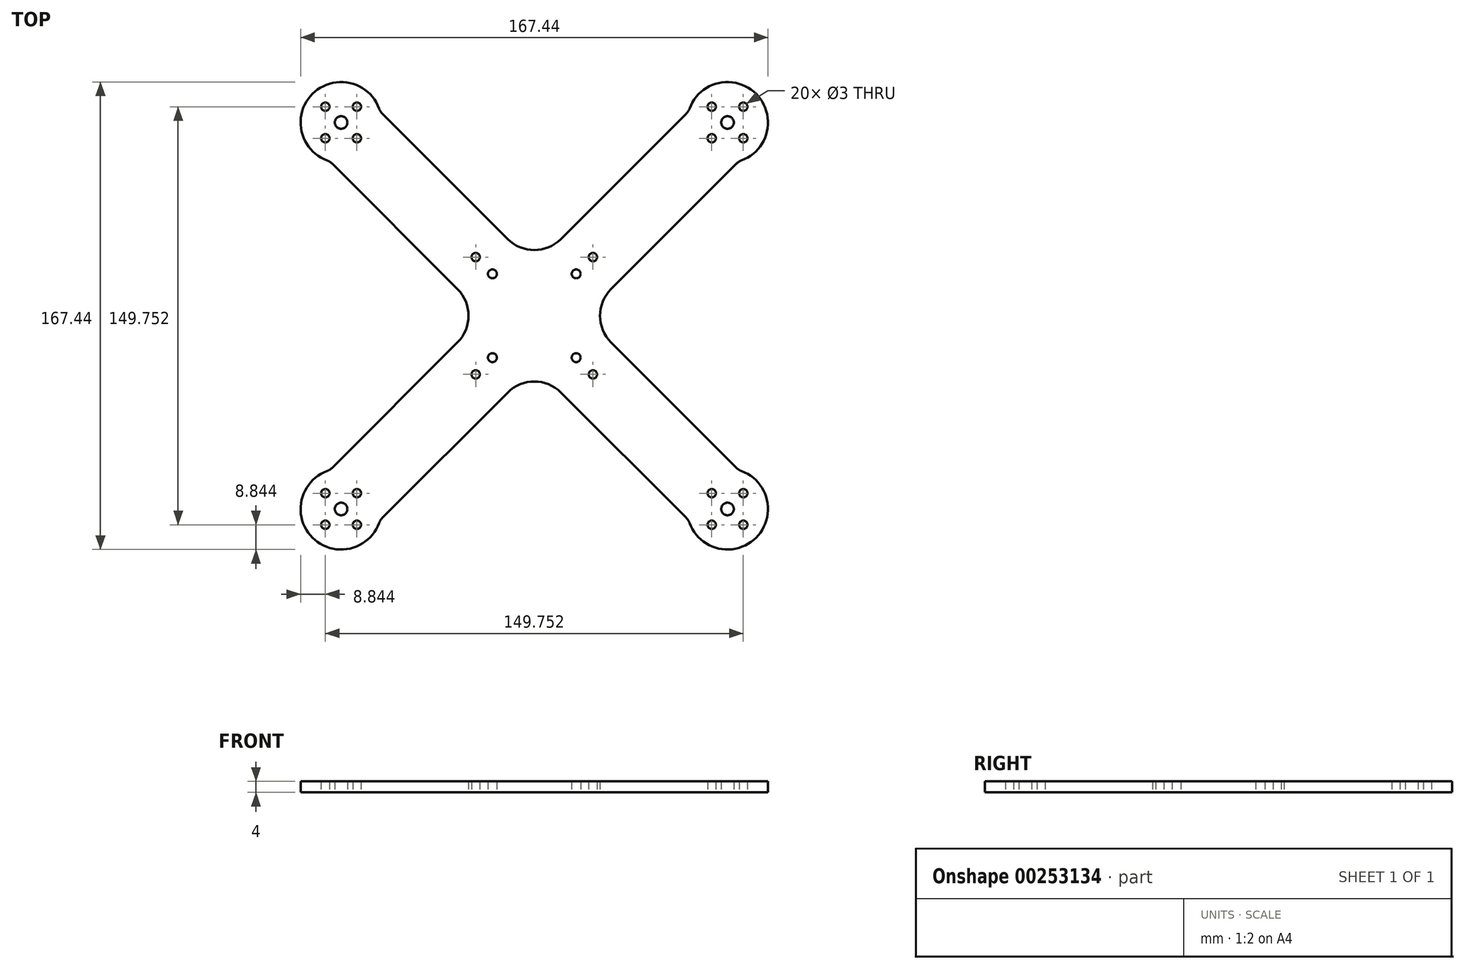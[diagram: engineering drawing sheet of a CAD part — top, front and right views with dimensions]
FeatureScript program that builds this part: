
annotation { "Feature Type Name" : "Feature", "Feature Type Description" : "" }
export const myFeature = defineFeature(function(context is Context, id is Id, definition is map)
    precondition{}
    {
        {
            var Q0;
            Q0=qCreatedBy(makeId("Top.planeOp"),FACE);
            var sketch = newSketch(context, id + "F0", { "sketchPlane" : qUnion([Q0])});
            skLineSegment(sketch, "E0.bottom", {"start": v(15, 15) * mm, "end": v(-15, 15) * mm, "construction": true});
            skLineSegment(sketch, "E0.left", {"start": v(15, 15) * mm, "end": v(15, -15) * mm, "construction": true});
            skLineSegment(sketch, "E0.right", {"start": v(-15, 15) * mm, "end": v(-15, -15) * mm, "construction": true});
            skCircle(sketch, "E1", {"center": v(-15, 15) * mm, "radius": 1.6 * mm});
            skCircle(sketch, "E2", {"center": v(15, 15) * mm, "radius": 1.6 * mm});
            skCircle(sketch, "E3", {"center": v(15, -15) * mm, "radius": 1.6 * mm});
            skCircle(sketch, "E4", {"center": v(-15, -15) * mm, "radius": 1.6 * mm});
            skLineSegment(sketch, "E5", {"start": v(-15, -15) * mm, "end": v(15, -15) * mm, "construction": true});
            skLineSegment(sketch, "E6", {"start": v(-15, 15) * mm, "end": v(15, -15) * mm, "construction": true});
            skLineSegment(sketch, "E7", {"start": v(-15, -15) * mm, "end": v(0, 0) * mm, "construction": true});
            skLineSegment(sketch, "E8.bottom", {"start": v(18, -18) * mm, "end": v(-18, -18) * mm, "construction": true});
            skLineSegment(sketch, "E8.top", {"start": v(18, 18) * mm, "end": v(-18, 18) * mm, "construction": true});
            skLineSegment(sketch, "E8.left", {"start": v(18, -18) * mm, "end": v(18, 18) * mm, "construction": true});
            skLineSegment(sketch, "E8.right", {"start": v(-18, -18) * mm, "end": v(-18, 18) * mm, "construction": true});
            skPoint(sketch, "E8.middle", {"position": v(0, 0) * mm});
            skLineSegment(sketch, "E9.bottom", {"start": v(21, 21) * mm, "end": v(-21, 21) * mm, "construction": true});
            skLineSegment(sketch, "E9.top", {"start": v(21, -21) * mm, "end": v(-21, -21) * mm, "construction": true});
            skLineSegment(sketch, "E9.left", {"start": v(21, 21) * mm, "end": v(21, -21) * mm, "construction": true});
            skLineSegment(sketch, "E9.right", {"start": v(-21, 21) * mm, "end": v(-21, -21) * mm, "construction": true});
            skCircle(sketch, "E10", {"center": v(21, 21) * mm, "radius": 1.5 * mm});
            skCircle(sketch, "E11", {"center": v(-21, 21) * mm, "radius": 1.5 * mm});
            skCircle(sketch, "E12", {"center": v(-21, -21) * mm, "radius": 1.5 * mm});
            skCircle(sketch, "E13", {"center": v(21, -21) * mm, "radius": 1.5 * mm});
            skPoint(sketch, "E14.visualSharp", {"position": v(-27.5, 27.5) * mm});
            skPoint(sketch, "E15.visualSharp", {"position": v(27.5, 27.5) * mm});
            skPoint(sketch, "E16.visualSharp", {"position": v(27.5, -27.5) * mm});
            skPoint(sketch, "E17.visualSharp", {"position": v(-27.5, -27.5) * mm});
            skLineSegment(sketch, "E18", {"start": v(-27.5, -27.5) * mm, "end": v(-69.22, -69.22) * mm, "construction": true});
            skCircle(sketch, "E19", {"center": v(-69.22, -69.22) * mm, "radius": 2.25 * mm});
            skLineSegment(sketch, "E20", {"start": v(-69.22, -69.22) * mm, "end": v(-63.56, -74.88) * mm, "construction": true});
            skLineSegment(sketch, "E21", {"start": v(-69.22, -69.22) * mm, "end": v(-74.88, -74.88) * mm, "construction": true});
            skLineSegment(sketch, "E22", {"start": v(-69.22, -69.22) * mm, "end": v(-74.88, -63.56) * mm, "construction": true});
            skCircle(sketch, "E23", {"center": v(-74.88, -63.56) * mm, "radius": 1.5 * mm});
            skCircle(sketch, "E24", {"center": v(-74.88, -74.88) * mm, "radius": 1.5 * mm});
            skCircle(sketch, "E25", {"center": v(-63.56, -74.88) * mm, "radius": 1.5 * mm});
            skCircle(sketch, "E26", {"center": v(-63.56, -63.56) * mm, "radius": 1.5 * mm});
            skArc(sketch, "E27", {"start": v(-74.22, -55.61) * mm, "mid": v(-79.47, -79.47) * mm, "end": v(-55.61, -74.22) * mm});
            skLineSegment(sketch, "E28.0", {"start": v(-27.5, -9.54) * mm, "end": v(-72.41, -54.45) * mm});
            skLineSegment(sketch, "E29.0", {"start": v(-9.54, -27.5) * mm, "end": v(-54.45, -72.41) * mm});
            skLineSegment(sketch, "E30.1.0", {"start": v(27.5, -9.54) * mm, "end": v(72.41, -54.45) * mm});
            skLineSegment(sketch, "E30.1.1", {"start": v(9.54, -27.5) * mm, "end": v(54.45, -72.41) * mm});
            skArc(sketch, "E30.1.2", {"start": v(55.61, -74.22) * mm, "mid": v(79.47, -79.47) * mm, "end": v(74.22, -55.61) * mm});
            skCircle(sketch, "E30.1.3", {"center": v(63.56, -74.88) * mm, "radius": 1.5 * mm});
            skCircle(sketch, "E30.1.4", {"center": v(63.56, -63.56) * mm, "radius": 1.5 * mm});
            skCircle(sketch, "E30.1.5", {"center": v(69.22, -69.22) * mm, "radius": 2.25 * mm});
            skCircle(sketch, "E30.1.6", {"center": v(74.88, -63.56) * mm, "radius": 1.5 * mm});
            skCircle(sketch, "E30.1.7", {"center": v(74.88, -74.88) * mm, "radius": 1.5 * mm});
            skLineSegment(sketch, "E30.1.8", {"start": v(69.22, -69.22) * mm, "end": v(74.88, -74.88) * mm, "construction": true});
            skLineSegment(sketch, "E30.1.9", {"start": v(69.22, -69.22) * mm, "end": v(63.56, -74.88) * mm, "construction": true});
            skLineSegment(sketch, "E30.1.10", {"start": v(27.5, -27.5) * mm, "end": v(69.22, -69.22) * mm, "construction": true});
            skLineSegment(sketch, "E30.1.11", {"start": v(69.22, -69.22) * mm, "end": v(74.88, -63.56) * mm, "construction": true});
            skLineSegment(sketch, "E30.2.0", {"start": v(9.54, 27.5) * mm, "end": v(54.45, 72.41) * mm});
            skLineSegment(sketch, "E30.2.1", {"start": v(27.5, 9.54) * mm, "end": v(72.41, 54.45) * mm});
            skArc(sketch, "E30.2.2", {"start": v(74.22, 55.61) * mm, "mid": v(79.47, 79.47) * mm, "end": v(55.61, 74.22) * mm});
            skCircle(sketch, "E30.2.3", {"center": v(74.88, 63.56) * mm, "radius": 1.5 * mm});
            skCircle(sketch, "E30.2.4", {"center": v(63.56, 63.56) * mm, "radius": 1.5 * mm});
            skCircle(sketch, "E30.2.5", {"center": v(69.22, 69.22) * mm, "radius": 2.25 * mm});
            skCircle(sketch, "E30.2.6", {"center": v(63.56, 74.88) * mm, "radius": 1.5 * mm});
            skCircle(sketch, "E30.2.7", {"center": v(74.88, 74.88) * mm, "radius": 1.5 * mm});
            skLineSegment(sketch, "E30.2.8", {"start": v(69.22, 69.22) * mm, "end": v(74.88, 74.88) * mm, "construction": true});
            skLineSegment(sketch, "E30.2.9", {"start": v(69.22, 69.22) * mm, "end": v(74.88, 63.56) * mm, "construction": true});
            skLineSegment(sketch, "E30.2.10", {"start": v(27.5, 27.5) * mm, "end": v(69.22, 69.22) * mm, "construction": true});
            skLineSegment(sketch, "E30.2.11", {"start": v(69.22, 69.22) * mm, "end": v(63.56, 74.88) * mm, "construction": true});
            skLineSegment(sketch, "E30.3.0", {"start": v(-27.5, 9.54) * mm, "end": v(-72.41, 54.45) * mm});
            skLineSegment(sketch, "E30.3.1", {"start": v(-9.54, 27.5) * mm, "end": v(-54.45, 72.41) * mm});
            skArc(sketch, "E30.3.2", {"start": v(-55.61, 74.22) * mm, "mid": v(-79.47, 79.47) * mm, "end": v(-74.22, 55.61) * mm});
            skCircle(sketch, "E30.3.3", {"center": v(-63.56, 74.88) * mm, "radius": 1.5 * mm});
            skCircle(sketch, "E30.3.4", {"center": v(-63.56, 63.56) * mm, "radius": 1.5 * mm});
            skCircle(sketch, "E30.3.5", {"center": v(-69.22, 69.22) * mm, "radius": 2.25 * mm});
            skCircle(sketch, "E30.3.6", {"center": v(-74.88, 63.56) * mm, "radius": 1.5 * mm});
            skCircle(sketch, "E30.3.7", {"center": v(-74.88, 74.88) * mm, "radius": 1.5 * mm});
            skLineSegment(sketch, "E30.3.8", {"start": v(-69.22, 69.22) * mm, "end": v(-74.88, 74.88) * mm, "construction": true});
            skLineSegment(sketch, "E30.3.9", {"start": v(-69.22, 69.22) * mm, "end": v(-63.56, 74.88) * mm, "construction": true});
            skLineSegment(sketch, "E30.3.10", {"start": v(-27.5, 27.5) * mm, "end": v(-69.22, 69.22) * mm, "construction": true});
            skLineSegment(sketch, "E30.3.11", {"start": v(-69.22, 69.22) * mm, "end": v(-74.88, 63.56) * mm, "construction": true});
            skArc(sketch, "E31", {"start": v(-27.5, -9.54) * mm, "mid": v(-23.55, 0) * mm, "end": v(-27.5, 9.54) * mm});
            skArc(sketch, "E32", {"start": v(27.5, 9.54) * mm, "mid": v(23.55, 0) * mm, "end": v(27.5, -9.54) * mm});
            skArc(sketch, "E33", {"start": v(-9.54, 27.5) * mm, "mid": v(0, 23.55) * mm, "end": v(9.54, 27.5) * mm});
            skArc(sketch, "E34", {"start": v(9.54, -27.5) * mm, "mid": v(0, -23.55) * mm, "end": v(-9.54, -27.5) * mm});
            skPoint(sketch, "E35.visualSharp", {"position": v(73.25, -55.3) * mm});
            skArc(sketch, "E35.filletArc", {"start": v(72.41, -54.45) * mm, "mid": v(73.26, -55.13) * mm, "end": v(74.22, -55.61) * mm});
            skPoint(sketch, "E36.visualSharp", {"position": v(55.3, -73.25) * mm});
            skArc(sketch, "E36.filletArc", {"start": v(55.61, -74.22) * mm, "mid": v(55.13, -73.26) * mm, "end": v(54.45, -72.41) * mm});
            skPoint(sketch, "E37.visualSharp", {"position": v(-55.3, -73.25) * mm});
            skArc(sketch, "E37.filletArc", {"start": v(-54.45, -72.41) * mm, "mid": v(-55.13, -73.26) * mm, "end": v(-55.61, -74.22) * mm});
            skPoint(sketch, "E38.visualSharp", {"position": v(-73.25, -55.3) * mm});
            skArc(sketch, "E38.filletArc", {"start": v(-74.22, -55.61) * mm, "mid": v(-73.26, -55.13) * mm, "end": v(-72.41, -54.45) * mm});
            skPoint(sketch, "E39.visualSharp", {"position": v(-73.25, 55.3) * mm});
            skArc(sketch, "E39.filletArc", {"start": v(-72.41, 54.45) * mm, "mid": v(-73.26, 55.13) * mm, "end": v(-74.22, 55.61) * mm});
            skPoint(sketch, "E40.visualSharp", {"position": v(-55.3, 73.25) * mm});
            skArc(sketch, "E40.filletArc", {"start": v(-55.61, 74.22) * mm, "mid": v(-55.13, 73.26) * mm, "end": v(-54.45, 72.41) * mm});
            skPoint(sketch, "E41.visualSharp", {"position": v(55.3, 73.25) * mm});
            skArc(sketch, "E41.filletArc", {"start": v(54.45, 72.41) * mm, "mid": v(55.13, 73.26) * mm, "end": v(55.61, 74.22) * mm});
            skPoint(sketch, "E42.visualSharp", {"position": v(73.25, 55.3) * mm});
            skArc(sketch, "E42.filletArc", {"start": v(74.22, 55.61) * mm, "mid": v(73.26, 55.13) * mm, "end": v(72.41, 54.45) * mm});
            skSolve(sketch);
        }
        {
            var Q0;
            Q0=makeQuery(id+"F0.imprint","IMPRINT",FACE,{"disambiguationData":[TD([[makeQuery(id+"F0.imprint","IMPRINT",EDGE,{"derivedFrom":sQuery(id+"F0.wireOp",EDGE,"E1")}),-1.0]])]});
            extrude(context, id + "F1", {"entities" : qUnion([Q0]), "depth" : 4 * mm});
        }
    });
